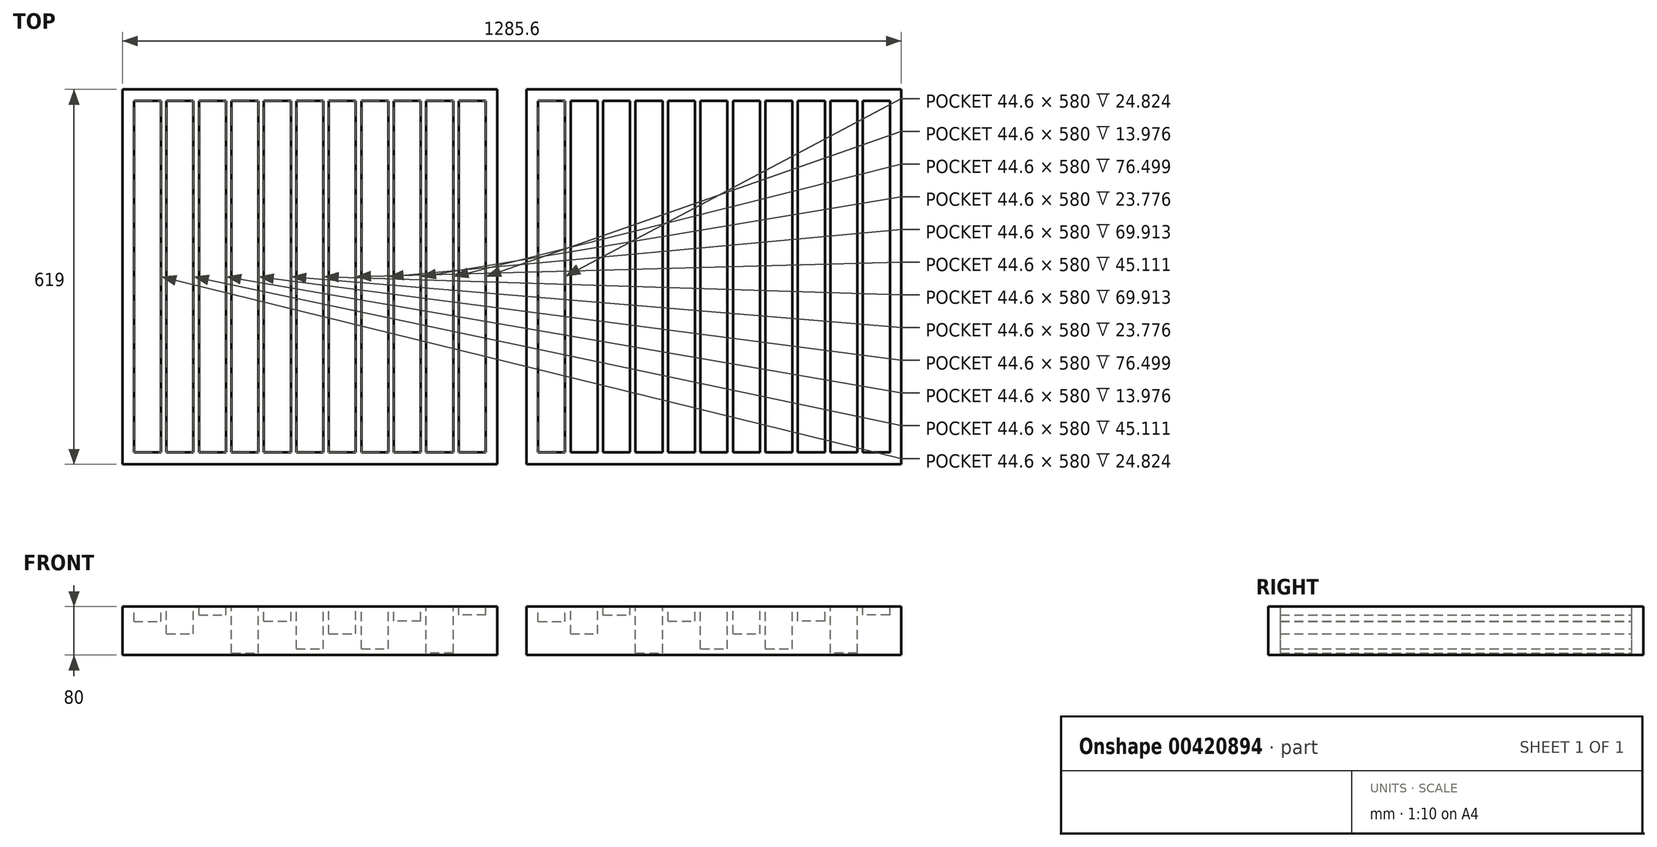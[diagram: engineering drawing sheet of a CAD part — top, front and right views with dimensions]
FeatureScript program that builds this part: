
annotation { "Feature Type Name" : "Feature", "Feature Type Description" : "" }
export const myFeature = defineFeature(function(context is Context, id is Id, definition is map)
    precondition{}
    {
        {
            var Q0;
            Q0=qCreatedBy(makeId("Front.planeOp"),FACE);
            var sketch = newSketch(context, id + "F0", { "sketchPlane" : qUnion([Q0])});
            skLineSegment(sketch, "E0.bottom", {"start": v(0, 0) * mm, "end": v(9, 0) * mm});
            skLineSegment(sketch, "E0.top", {"start": v(0, 80) * mm, "end": v(9, 80) * mm});
            skLineSegment(sketch, "E0.left", {"start": v(0, 0) * mm, "end": v(0, 80) * mm});
            skLineSegment(sketch, "E0.right", {"start": v(9, 0) * mm, "end": v(9, 80) * mm});
            skLineSegment(sketch, "E1.1.0.0", {"start": v(53.6, 80) * mm, "end": v(62.6, 80) * mm});
            skLineSegment(sketch, "E1.1.0.1", {"start": v(62.6, 0) * mm, "end": v(62.6, 80) * mm});
            skLineSegment(sketch, "E1.1.0.2", {"start": v(53.6, 0) * mm, "end": v(62.6, 0) * mm});
            skLineSegment(sketch, "E1.1.0.3", {"start": v(53.6, 0) * mm, "end": v(53.6, 80) * mm});
            skLineSegment(sketch, "E1.2.0.0", {"start": v(107.2, 80) * mm, "end": v(116.2, 80) * mm});
            skLineSegment(sketch, "E1.2.0.1", {"start": v(116.2, 0) * mm, "end": v(116.2, 80) * mm});
            skLineSegment(sketch, "E1.2.0.2", {"start": v(107.2, 0) * mm, "end": v(116.2, 0) * mm});
            skLineSegment(sketch, "E1.2.0.3", {"start": v(107.2, 0) * mm, "end": v(107.2, 80) * mm});
            skLineSegment(sketch, "E1.3.0.0", {"start": v(160.8, 80) * mm, "end": v(169.8, 80) * mm});
            skLineSegment(sketch, "E1.3.0.1", {"start": v(169.8, 0) * mm, "end": v(169.8, 80) * mm});
            skLineSegment(sketch, "E1.3.0.2", {"start": v(160.8, 0) * mm, "end": v(169.8, 0) * mm});
            skLineSegment(sketch, "E1.3.0.3", {"start": v(160.8, 0) * mm, "end": v(160.8, 80) * mm});
            skLineSegment(sketch, "E1.4.0.0", {"start": v(214.4, 80) * mm, "end": v(223.4, 80) * mm});
            skLineSegment(sketch, "E1.4.0.1", {"start": v(223.4, 0) * mm, "end": v(223.4, 80) * mm});
            skLineSegment(sketch, "E1.4.0.2", {"start": v(214.4, 0) * mm, "end": v(223.4, 0) * mm});
            skLineSegment(sketch, "E1.4.0.3", {"start": v(214.4, 0) * mm, "end": v(214.4, 80) * mm});
            skLineSegment(sketch, "E1.5.0.0", {"start": v(268, 80) * mm, "end": v(277, 80) * mm});
            skLineSegment(sketch, "E1.5.0.1", {"start": v(277, 0) * mm, "end": v(277, 80) * mm});
            skLineSegment(sketch, "E1.5.0.2", {"start": v(268, 0) * mm, "end": v(277, 0) * mm});
            skLineSegment(sketch, "E1.5.0.3", {"start": v(268, 0) * mm, "end": v(268, 80) * mm});
            skLineSegment(sketch, "E1.6.0.0", {"start": v(321.6, 80) * mm, "end": v(330.6, 80) * mm});
            skLineSegment(sketch, "E1.6.0.1", {"start": v(330.6, 0) * mm, "end": v(330.6, 80) * mm});
            skLineSegment(sketch, "E1.6.0.2", {"start": v(321.6, 0) * mm, "end": v(330.6, 0) * mm});
            skLineSegment(sketch, "E1.6.0.3", {"start": v(321.6, 0) * mm, "end": v(321.6, 80) * mm});
            skLineSegment(sketch, "E1.7.0.0", {"start": v(375.2, 80) * mm, "end": v(384.2, 80) * mm});
            skLineSegment(sketch, "E1.7.0.1", {"start": v(384.2, 0) * mm, "end": v(384.2, 80) * mm});
            skLineSegment(sketch, "E1.7.0.2", {"start": v(375.2, 0) * mm, "end": v(384.2, 0) * mm});
            skLineSegment(sketch, "E1.7.0.3", {"start": v(375.2, 0) * mm, "end": v(375.2, 80) * mm});
            skLineSegment(sketch, "E1.8.0.0", {"start": v(428.8, 80) * mm, "end": v(437.8, 80) * mm});
            skLineSegment(sketch, "E1.8.0.1", {"start": v(437.8, 0) * mm, "end": v(437.8, 80) * mm});
            skLineSegment(sketch, "E1.8.0.2", {"start": v(428.8, 0) * mm, "end": v(437.8, 0) * mm});
            skLineSegment(sketch, "E1.8.0.3", {"start": v(428.8, 0) * mm, "end": v(428.8, 80) * mm});
            skLineSegment(sketch, "E1.9.0.0", {"start": v(482.4, 80) * mm, "end": v(491.4, 80) * mm});
            skLineSegment(sketch, "E1.9.0.1", {"start": v(491.4, 0) * mm, "end": v(491.4, 80) * mm});
            skLineSegment(sketch, "E1.9.0.2", {"start": v(482.4, 0) * mm, "end": v(491.4, 0) * mm});
            skLineSegment(sketch, "E1.9.0.3", {"start": v(482.4, 0) * mm, "end": v(482.4, 80) * mm});
            skLineSegment(sketch, "E1.10.0.0", {"start": v(536, 80) * mm, "end": v(545, 80) * mm});
            skLineSegment(sketch, "E1.10.0.1", {"start": v(545, 0) * mm, "end": v(545, 80) * mm});
            skLineSegment(sketch, "E1.10.0.2", {"start": v(536, 0) * mm, "end": v(545, 0) * mm});
            skLineSegment(sketch, "E1.10.0.3", {"start": v(536, 0) * mm, "end": v(536, 80) * mm});
            skLineSegment(sketch, "E1.11.0.0", {"start": v(589.6, 80) * mm, "end": v(598.6, 80) * mm});
            skLineSegment(sketch, "E1.11.0.1", {"start": v(598.6, 0) * mm, "end": v(598.6, 80) * mm});
            skLineSegment(sketch, "E1.11.0.2", {"start": v(589.6, 0) * mm, "end": v(598.6, 0) * mm});
            skLineSegment(sketch, "E1.11.0.3", {"start": v(589.6, 0) * mm, "end": v(589.6, 80) * mm});
            skLineSegment(sketch, "E1.direction1", {"start": v(0, 0) * mm, "end": v(53.6, 0) * mm, "construction": true});
            skLineSegment(sketch, "E2", {"start": v(9, 55.18) * mm, "end": v(53.6, 55.18) * mm});
            skLineSegment(sketch, "E3", {"start": v(62.6, 34.89) * mm, "end": v(107.2, 34.89) * mm});
            skLineSegment(sketch, "E4", {"start": v(116.2, 66.02) * mm, "end": v(160.8, 66.02) * mm});
            skLineSegment(sketch, "E5", {"start": v(169.8, 3.5) * mm, "end": v(214.4, 3.5) * mm});
            skLineSegment(sketch, "E6", {"start": v(223.4, 56.22) * mm, "end": v(268, 56.22) * mm});
            skLineSegment(sketch, "E7", {"start": v(589.6, 66.02) * mm, "end": v(545, 66.02) * mm});
            skLineSegment(sketch, "E8", {"start": v(536, 3.5) * mm, "end": v(491.4, 3.5) * mm});
            skPoint(sketch, "E8.startSnap0", {"position": v(192.1, 3.5) * mm});
            skLineSegment(sketch, "E9", {"start": v(482.4, 56.22) * mm, "end": v(437.8, 56.22) * mm});
            skLineSegment(sketch, "E10", {"start": v(330.6, 34.89) * mm, "end": v(375.2, 34.89) * mm});
            skLineSegment(sketch, "E11", {"start": v(277, 10.09) * mm, "end": v(321.6, 10.09) * mm});
            skLineSegment(sketch, "E12", {"start": v(384.2, 10.09) * mm, "end": v(428.8, 10.09) * mm});
            skLineSegment(sketch, "E13", {"start": v(0, 0) * mm, "end": v(598.6, 0) * mm});
            skLineSegment(sketch, "E14", {"start": v(0, 80) * mm, "end": v(598.6, 80) * mm});
            skSolve(sketch);
        }
        {
            var Q0;
            {var subQ3=sQuery(id+"F0.wireOp",EDGE,"E11");Q0=makeQuery(id+"F0.imprint","IMPRINT",FACE,{"disambiguationData":[TD([[makeQuery(id+"F0.imprint","IMPRINT",EDGE,{"derivedFrom":subQ3}),-1.0]])]});}
            var Q1;
            {var subQ6=sQuery(id+"F0.wireOp",EDGE,"E0.left");Q1=makeQuery(id+"F0.imprint","IMPRINT",FACE,{"disambiguationData":[TD([[makeQuery(id+"F0.imprint","IMPRINT",EDGE,{"derivedFrom":subQ6}),-1.0]])]});}
            var Q2;
            {var subQ3=sQuery(id+"F0.wireOp",EDGE,"E2");Q2=makeQuery(id+"F0.imprint","IMPRINT",FACE,{"disambiguationData":[TD([[makeQuery(id+"F0.imprint","IMPRINT",EDGE,{"derivedFrom":subQ3}),-1.0]])]});}
            var Q3;
            {var subQ4=sQuery(id+"F0.wireOp",EDGE,"RwyZLAWs-IkjT-xB0i-7LVW-v5MOJDuku8NZ");var subQ6=sQuery(id+"F0.wireOp",EDGE,"E1.1.0.1");var subQ7=makeQuery(id+"F0.imprint","INTERSECT",VERTEX,{"derivedFrom":[subQ6,subQ4]});Q3=makeQuery(id+"F0.imprint","IMPRINT",FACE,{"disambiguationData":[TD([[makeQuery(id+"F0.imprint","IMPRINT",EDGE,{"disambiguationData":[TD([[subQ7,-1.0]])],"derivedFrom":subQ6}),1.0]])]});}
            var Q4;
            {var subQ3=sQuery(id+"F0.wireOp",EDGE,"E3");Q4=makeQuery(id+"F0.imprint","IMPRINT",FACE,{"disambiguationData":[TD([[makeQuery(id+"F0.imprint","IMPRINT",EDGE,{"derivedFrom":subQ3}),-1.0]])]});}
            var Q5;
            {var subQ4=sQuery(id+"F0.wireOp",EDGE,"RwyZLAWs-IkjT-xB0i-7LVW-v5MOJDuku8NZ");var subQ6=sQuery(id+"F0.wireOp",EDGE,"E1.2.0.1");var subQ9=makeQuery(id+"F0.imprint","INTERSECT",VERTEX,{"derivedFrom":[subQ6,subQ4]});Q5=makeQuery(id+"F0.imprint","IMPRINT",FACE,{"disambiguationData":[TD([[makeQuery(id+"F0.imprint","IMPRINT",EDGE,{"disambiguationData":[TD([[subQ9,-1.0]])],"derivedFrom":subQ6}),1.0]])]});}
            var Q6;
            {var subQ3=sQuery(id+"F0.wireOp",EDGE,"E4");Q6=makeQuery(id+"F0.imprint","IMPRINT",FACE,{"disambiguationData":[TD([[makeQuery(id+"F0.imprint","IMPRINT",EDGE,{"derivedFrom":subQ3}),-1.0]])]});}
            var Q7;
            {var subQ4=sQuery(id+"F0.wireOp",EDGE,"E1.3.0.1");var subQ6=sQuery(id+"F0.wireOp",EDGE,"RwyZLAWs-IkjT-xB0i-7LVW-v5MOJDuku8NZ");var subQ9=makeQuery(id+"F0.imprint","INTERSECT",VERTEX,{"derivedFrom":[subQ4,subQ6]});Q7=makeQuery(id+"F0.imprint","IMPRINT",FACE,{"disambiguationData":[TD([[makeQuery(id+"F0.imprint","IMPRINT",EDGE,{"disambiguationData":[TD([[subQ9,-1.0]])],"derivedFrom":subQ4}),1.0]])]});}
            var Q8;
            {var subQ3=sQuery(id+"F0.wireOp",EDGE,"E5");Q8=makeQuery(id+"F0.imprint","IMPRINT",FACE,{"disambiguationData":[TD([[makeQuery(id+"F0.imprint","IMPRINT",EDGE,{"derivedFrom":subQ3}),-1.0]])]});}
            var Q9;
            {var subQ4=sQuery(id+"F0.wireOp",EDGE,"RwyZLAWs-IkjT-xB0i-7LVW-v5MOJDuku8NZ");var subQ6=sQuery(id+"F0.wireOp",EDGE,"E1.4.0.1");var subQ9=makeQuery(id+"F0.imprint","INTERSECT",VERTEX,{"derivedFrom":[subQ6,subQ4]});Q9=makeQuery(id+"F0.imprint","IMPRINT",FACE,{"disambiguationData":[TD([[makeQuery(id+"F0.imprint","IMPRINT",EDGE,{"disambiguationData":[TD([[subQ9,-1.0]])],"derivedFrom":subQ6}),1.0]])]});}
            var Q10;
            {var subQ3=sQuery(id+"F0.wireOp",EDGE,"E6");Q10=makeQuery(id+"F0.imprint","IMPRINT",FACE,{"disambiguationData":[TD([[makeQuery(id+"F0.imprint","IMPRINT",EDGE,{"derivedFrom":subQ3}),-1.0]])]});}
            var Q11;
            {var subQ4=sQuery(id+"F0.wireOp",EDGE,"RwyZLAWs-IkjT-xB0i-7LVW-v5MOJDuku8NZ");var subQ6=sQuery(id+"F0.wireOp",EDGE,"E1.5.0.1");var subQ9=makeQuery(id+"F0.imprint","INTERSECT",VERTEX,{"derivedFrom":[subQ6,subQ4]});Q11=makeQuery(id+"F0.imprint","IMPRINT",FACE,{"disambiguationData":[TD([[makeQuery(id+"F0.imprint","IMPRINT",EDGE,{"disambiguationData":[TD([[subQ9,-1.0]])],"derivedFrom":subQ6}),1.0]])]});}
            var Q12;
            {var subQ4=sQuery(id+"F0.wireOp",EDGE,"RwyZLAWs-IkjT-xB0i-7LVW-v5MOJDuku8NZ");var subQ5=sQuery(id+"F0.wireOp",EDGE,"E1.6.0.1");var subQ6=makeQuery(id+"F0.imprint","INTERSECT",VERTEX,{"derivedFrom":[subQ5,subQ4]});Q12=makeQuery(id+"F0.imprint","IMPRINT",FACE,{"disambiguationData":[TD([[makeQuery(id+"F0.imprint","IMPRINT",EDGE,{"disambiguationData":[TD([[subQ6,-1.0]])],"derivedFrom":subQ5}),1.0]])]});}
            var Q13;
            {var subQ3=sQuery(id+"F0.wireOp",EDGE,"E10");Q13=makeQuery(id+"F0.imprint","IMPRINT",FACE,{"disambiguationData":[TD([[makeQuery(id+"F0.imprint","IMPRINT",EDGE,{"derivedFrom":subQ3}),-1.0]])]});}
            var Q14;
            {var subQ4=sQuery(id+"F0.wireOp",EDGE,"RwyZLAWs-IkjT-xB0i-7LVW-v5MOJDuku8NZ");var subQ6=sQuery(id+"F0.wireOp",EDGE,"E1.7.0.1");var subQ9=makeQuery(id+"F0.imprint","INTERSECT",VERTEX,{"derivedFrom":[subQ6,subQ4]});Q14=makeQuery(id+"F0.imprint","IMPRINT",FACE,{"disambiguationData":[TD([[makeQuery(id+"F0.imprint","IMPRINT",EDGE,{"disambiguationData":[TD([[subQ9,-1.0]])],"derivedFrom":subQ6}),1.0]])]});}
            var Q15;
            {var subQ4=sQuery(id+"F0.wireOp",EDGE,"RwyZLAWs-IkjT-xB0i-7LVW-v5MOJDuku8NZ");var subQ6=sQuery(id+"F0.wireOp",EDGE,"E1.8.0.1");var subQ9=makeQuery(id+"F0.imprint","INTERSECT",VERTEX,{"derivedFrom":[subQ6,subQ4]});Q15=makeQuery(id+"F0.imprint","IMPRINT",FACE,{"disambiguationData":[TD([[makeQuery(id+"F0.imprint","IMPRINT",EDGE,{"disambiguationData":[TD([[subQ9,-1.0]])],"derivedFrom":subQ6}),1.0]])]});}
            var Q16;
            {var subQ3=sQuery(id+"F0.wireOp",EDGE,"E9");Q16=makeQuery(id+"F0.imprint","IMPRINT",FACE,{"disambiguationData":[TD([[makeQuery(id+"F0.imprint","IMPRINT",EDGE,{"derivedFrom":subQ3}),1.0]])]});}
            var Q17;
            {var subQ4=sQuery(id+"F0.wireOp",EDGE,"RwyZLAWs-IkjT-xB0i-7LVW-v5MOJDuku8NZ");var subQ6=sQuery(id+"F0.wireOp",EDGE,"E1.9.0.1");var subQ9=makeQuery(id+"F0.imprint","INTERSECT",VERTEX,{"derivedFrom":[subQ6,subQ4]});Q17=makeQuery(id+"F0.imprint","IMPRINT",FACE,{"disambiguationData":[TD([[makeQuery(id+"F0.imprint","IMPRINT",EDGE,{"disambiguationData":[TD([[subQ9,-1.0]])],"derivedFrom":subQ6}),1.0]])]});}
            var Q18;
            {var subQ3=sQuery(id+"F0.wireOp",EDGE,"E8");Q18=makeQuery(id+"F0.imprint","IMPRINT",FACE,{"disambiguationData":[TD([[makeQuery(id+"F0.imprint","IMPRINT",EDGE,{"derivedFrom":subQ3}),1.0]])]});}
            var Q19;
            {var subQ4=sQuery(id+"F0.wireOp",EDGE,"RwyZLAWs-IkjT-xB0i-7LVW-v5MOJDuku8NZ");var subQ6=sQuery(id+"F0.wireOp",EDGE,"E1.10.0.1");var subQ9=makeQuery(id+"F0.imprint","INTERSECT",VERTEX,{"derivedFrom":[subQ6,subQ4]});Q19=makeQuery(id+"F0.imprint","IMPRINT",FACE,{"disambiguationData":[TD([[makeQuery(id+"F0.imprint","IMPRINT",EDGE,{"disambiguationData":[TD([[subQ9,-1.0]])],"derivedFrom":subQ6}),1.0]])]});}
            var Q20;
            {var subQ3=sQuery(id+"F0.wireOp",EDGE,"E7");Q20=makeQuery(id+"F0.imprint","IMPRINT",FACE,{"disambiguationData":[TD([[makeQuery(id+"F0.imprint","IMPRINT",EDGE,{"derivedFrom":subQ3}),1.0]])]});}
            var Q21;
            {var subQ4=sQuery(id+"F0.wireOp",EDGE,"RwyZLAWs-IkjT-xB0i-7LVW-v5MOJDuku8NZ");var subQ6=sQuery(id+"F0.wireOp",EDGE,"E1.11.0.1");var subQ9=makeQuery(id+"F0.imprint","INTERSECT",VERTEX,{"derivedFrom":[subQ6,subQ4]});Q21=makeQuery(id+"F0.imprint","IMPRINT",FACE,{"disambiguationData":[TD([[makeQuery(id+"F0.imprint","IMPRINT",EDGE,{"disambiguationData":[TD([[subQ9,-1.0]])],"derivedFrom":subQ6}),1.0]])]});}
            var Q22;
            {var subQ3=sQuery(id+"F0.wireOp",EDGE,"QDkUnuJY-H8uB-LQRV-5p4X-Az3B3ou244IQ");Q22=makeQuery(id+"F0.imprint","IMPRINT",FACE,{"disambiguationData":[TD([[makeQuery(id+"F0.imprint","IMPRINT",EDGE,{"derivedFrom":subQ3}),1.0]])]});}
            var Q23;
            {var subQ4=sQuery(id+"F0.wireOp",EDGE,"c455265c-4ce7-41d5-8e05-9c11a3bf2246.3.11.0");var subQ6=sQuery(id+"F0.wireOp",EDGE,"RwyZLAWs-IkjT-xB0i-7LVW-v5MOJDuku8NZ");var subQ9=makeQuery(id+"F0.imprint","INTERSECT",VERTEX,{"derivedFrom":[subQ4,subQ6]});Q23=makeQuery(id+"F0.imprint","IMPRINT",FACE,{"disambiguationData":[TD([[makeQuery(id+"F0.imprint","IMPRINT",EDGE,{"disambiguationData":[TD([[subQ9,-1.0]])],"derivedFrom":subQ4}),1.0]])]});}
            var Q24;
            {var subQ3=sQuery(id+"F0.wireOp",EDGE,"WxUK2kOJ-jrxP-pgZT-nzD5-Vg9UTsvjE4ji");Q24=makeQuery(id+"F0.imprint","IMPRINT",FACE,{"disambiguationData":[TD([[makeQuery(id+"F0.imprint","IMPRINT",EDGE,{"derivedFrom":subQ3}),-1.0]])]});}
            var Q25;
            {var subQ1=sQuery(id+"F0.wireOp",EDGE,"6b18c773-8643-46cd-9ae8-48085646cfae.3.12.0");Q25=makeQuery(id+"F0.imprint","IMPRINT",FACE,{"disambiguationData":[TD([[makeQuery(id+"F0.imprint","IMPRINT",EDGE,{"derivedFrom":subQ1}),1.0]])]});}
            var Q26;
            {var subQ3=sQuery(id+"F0.wireOp",EDGE,"E12");Q26=makeQuery(id+"F0.imprint","IMPRINT",FACE,{"disambiguationData":[TD([[makeQuery(id+"F0.imprint","IMPRINT",EDGE,{"derivedFrom":subQ3}),-1.0]])]});}
            extrude(context, id + "F1", {"entities" : qUnion([Q0, Q1, Q2, Q3, Q4, Q5, Q6, Q7, Q8, Q9, Q10, Q11, Q12, Q13, Q14, Q15, Q16, Q17, Q18, Q19, Q20, Q21, Q22, Q23, Q24, Q25, Q26]), "depth" : 580 * mm});
        }
        {
            var Q0;
            Q0 = qSketchRegion(id + "F0", true);
            extrude(context, id + "F2", {"entities" : qUnion([Q0]), "operationType" : NewBodyOperationType.ADD, "oppositeDirection" : true, "depth" : 9 * mm});
        }
        {
            var Q0;
            Q0 = qSketchRegion(id + "F0", true);
            var Q1;
            Q1=makeQuery(id+"F1.opExtrude","CAP_VERTEX",VERTEX,{"disambiguationData":[OSD([sQuery(id+"F0.wireOp",EDGE,"E0.left"),sQuery(id+"F0.wireOp",EDGE,"bcZIO9kF-9Tbn-Df1j-lN5f-S5Wp7413Y2EX")])],"isStart":false});
            extrude(context, id + "F3", {"entities" : qUnion([Q0]), "operationType" : NewBodyOperationType.ADD, "endBoundEntityVertex" : qUnion([Q1]), "depth" : 590 * mm, "hasSecondDirection" : true, "secondDirectionOppositeDirection" : false, "secondDirectionDepth" : 580 * mm});
        }
        {
            var Q0;
            {var subQ0=sQuery(id+"F0.wireOp",EDGE,"E14");Q0=makeQuery(id+"F3.boolean.opBoolean","MERGE",FACE,{"derivedFrom":[makeQuery(id+"F2.boolean.opBoolean","MERGE",FACE,{"derivedFrom":[makeQuery(id+"F1.opExtrude","SWEPT_FACE",FACE,{"disambiguationData":[OSD([subQ0]),TDD([makeQuery(id+"F0.imprint","IMPRINT",EDGE,{"disambiguationData":[TD([[makeQuery(id+"F0.imprint","INTERSECT",VERTEX,{"derivedFrom":[sQuery(id+"F0.wireOp",EDGE,"E0.left"),subQ0]}),-1.0]])],"derivedFrom":subQ0})])]}),makeQuery(id+"F1.opExtrude","SWEPT_FACE",FACE,{"disambiguationData":[OSD([subQ0]),TDD([makeQuery(id+"F0.imprint","IMPRINT",EDGE,{"disambiguationData":[TD([[makeQuery(id+"F0.imprint","INTERSECT",VERTEX,{"derivedFrom":[sQuery(id+"F0.wireOp",EDGE,"E1.1.0.1"),subQ0]}),1.0]])],"derivedFrom":subQ0})])]}),makeQuery(id+"F1.opExtrude","SWEPT_FACE",FACE,{"disambiguationData":[OSD([subQ0]),TDD([makeQuery(id+"F0.imprint","IMPRINT",EDGE,{"disambiguationData":[TD([[makeQuery(id+"F0.imprint","INTERSECT",VERTEX,{"derivedFrom":[sQuery(id+"F0.wireOp",EDGE,"E1.2.0.1"),subQ0]}),1.0]])],"derivedFrom":subQ0})])]}),makeQuery(id+"F1.opExtrude","SWEPT_FACE",FACE,{"disambiguationData":[OSD([subQ0]),TDD([makeQuery(id+"F0.imprint","IMPRINT",EDGE,{"disambiguationData":[TD([[makeQuery(id+"F0.imprint","INTERSECT",VERTEX,{"derivedFrom":[sQuery(id+"F0.wireOp",EDGE,"E1.3.0.1"),subQ0]}),1.0]])],"derivedFrom":subQ0})])]}),makeQuery(id+"F1.opExtrude","SWEPT_FACE",FACE,{"disambiguationData":[OSD([subQ0]),TDD([makeQuery(id+"F0.imprint","IMPRINT",EDGE,{"disambiguationData":[TD([[makeQuery(id+"F0.imprint","INTERSECT",VERTEX,{"derivedFrom":[sQuery(id+"F0.wireOp",EDGE,"E1.4.0.1"),subQ0]}),1.0]])],"derivedFrom":subQ0})])]}),makeQuery(id+"F1.opExtrude","SWEPT_FACE",FACE,{"disambiguationData":[OSD([subQ0]),TDD([makeQuery(id+"F0.imprint","IMPRINT",EDGE,{"disambiguationData":[TD([[makeQuery(id+"F0.imprint","INTERSECT",VERTEX,{"derivedFrom":[sQuery(id+"F0.wireOp",EDGE,"E1.5.0.1"),subQ0]}),1.0]])],"derivedFrom":subQ0})])]}),makeQuery(id+"F1.opExtrude","SWEPT_FACE",FACE,{"disambiguationData":[OSD([subQ0]),TDD([makeQuery(id+"F0.imprint","IMPRINT",EDGE,{"disambiguationData":[TD([[makeQuery(id+"F0.imprint","INTERSECT",VERTEX,{"derivedFrom":[sQuery(id+"F0.wireOp",EDGE,"E1.6.0.1"),subQ0]}),1.0]])],"derivedFrom":subQ0})])]}),makeQuery(id+"F1.opExtrude","SWEPT_FACE",FACE,{"disambiguationData":[OSD([subQ0]),TDD([makeQuery(id+"F0.imprint","IMPRINT",EDGE,{"disambiguationData":[TD([[makeQuery(id+"F0.imprint","INTERSECT",VERTEX,{"derivedFrom":[sQuery(id+"F0.wireOp",EDGE,"E1.7.0.1"),subQ0]}),1.0]])],"derivedFrom":subQ0})])]}),makeQuery(id+"F1.opExtrude","SWEPT_FACE",FACE,{"disambiguationData":[OSD([subQ0]),TDD([makeQuery(id+"F0.imprint","IMPRINT",EDGE,{"disambiguationData":[TD([[makeQuery(id+"F0.imprint","INTERSECT",VERTEX,{"derivedFrom":[sQuery(id+"F0.wireOp",EDGE,"E1.8.0.1"),subQ0]}),1.0]])],"derivedFrom":subQ0})])]}),makeQuery(id+"F1.opExtrude","SWEPT_FACE",FACE,{"disambiguationData":[OSD([subQ0]),TDD([makeQuery(id+"F0.imprint","IMPRINT",EDGE,{"disambiguationData":[TD([[makeQuery(id+"F0.imprint","INTERSECT",VERTEX,{"derivedFrom":[sQuery(id+"F0.wireOp",EDGE,"E1.9.0.1"),subQ0]}),1.0]])],"derivedFrom":subQ0})])]}),makeQuery(id+"F1.opExtrude","SWEPT_FACE",FACE,{"disambiguationData":[OSD([subQ0]),TDD([makeQuery(id+"F0.imprint","IMPRINT",EDGE,{"disambiguationData":[TD([[makeQuery(id+"F0.imprint","INTERSECT",VERTEX,{"derivedFrom":[sQuery(id+"F0.wireOp",EDGE,"E1.10.0.1"),subQ0]}),1.0]])],"derivedFrom":subQ0})])]}),makeQuery(id+"F1.opExtrude","SWEPT_FACE",FACE,{"disambiguationData":[OSD([subQ0]),TDD([makeQuery(id+"F0.imprint","IMPRINT",EDGE,{"disambiguationData":[TD([[makeQuery(id+"F0.imprint","INTERSECT",VERTEX,{"derivedFrom":[sQuery(id+"F0.wireOp",EDGE,"E1.11.0.1"),subQ0]}),1.0]])],"derivedFrom":subQ0})])]}),makeQuery(id+"F2.opExtrude","SWEPT_FACE",FACE,{"disambiguationData":[OSD([subQ0])]})]}),makeQuery(id+"F3.opExtrude","SWEPT_FACE",FACE,{"disambiguationData":[OSD([subQ0])]})]});}
            var sketch = newSketch(context, id + "F4", { "sketchPlane" : qUnion([Q0])});
            skLineSegment(sketch, "E15.0", {"start": v(598.6, -590) * mm, "end": v(598.6, 9) * mm});
            skLineSegment(sketch, "E16.0", {"start": v(0, -590) * mm, "end": v(598.6, -590) * mm});
            skLineSegment(sketch, "E17.0", {"start": v(0, -590) * mm, "end": v(0, 9) * mm});
            skLineSegment(sketch, "E18.0", {"start": v(0, 9) * mm, "end": v(598.6, 9) * mm});
            skLineSegment(sketch, "E19.0", {"start": v(608.6, -600) * mm, "end": v(608.6, 19) * mm});
            skLineSegment(sketch, "E19.1", {"start": v(-10, -600) * mm, "end": v(608.6, -600) * mm});
            skLineSegment(sketch, "E19.2", {"start": v(-10, -600) * mm, "end": v(-10, 19) * mm});
            skLineSegment(sketch, "E19.3", {"start": v(-10, 19) * mm, "end": v(608.6, 19) * mm});
            skSolve(sketch);
        }
        {
            var Q0;
            Q0 = qSketchRegion(id + "F4", true);
            var Q1;
            Q1=makeQuery(id+"F3.opExtrude","CAP_VERTEX",VERTEX,{"disambiguationData":[OSD([sQuery(id+"F0.wireOp",EDGE,"E0.left"),sQuery(id+"F0.wireOp",EDGE,"E13")])],"isStart":false});
            extrude(context, id + "F5", {"entities" : qUnion([Q0]), "operationType" : NewBodyOperationType.ADD, "endBound" : BoundingType.UP_TO_VERTEX, "oppositeDirection" : true, "endBoundEntityVertex" : qUnion([Q1]), "depth" : 25 * mm});
        }
        {
            var Q0;
            Q0=makeQuery(id+"F1.opExtrude","SWEPT_BODY",BODY,{"disambiguationData":[OSD([sQuery(id+"F0.wireOp",EDGE,"E0.left"),sQuery(id+"F0.wireOp",EDGE,"E0.right"),sQuery(id+"F0.wireOp",EDGE,"E1.1.0.1"),sQuery(id+"F0.wireOp",EDGE,"E1.1.0.3"),sQuery(id+"F0.wireOp",EDGE,"E1.2.0.1"),sQuery(id+"F0.wireOp",EDGE,"E1.2.0.3"),sQuery(id+"F0.wireOp",EDGE,"E1.3.0.1"),sQuery(id+"F0.wireOp",EDGE,"E1.3.0.3"),sQuery(id+"F0.wireOp",EDGE,"E1.4.0.1"),sQuery(id+"F0.wireOp",EDGE,"E1.4.0.3"),sQuery(id+"F0.wireOp",EDGE,"E1.5.0.1"),sQuery(id+"F0.wireOp",EDGE,"E1.5.0.3"),sQuery(id+"F0.wireOp",EDGE,"E1.6.0.1"),sQuery(id+"F0.wireOp",EDGE,"E1.6.0.3"),sQuery(id+"F0.wireOp",EDGE,"E1.7.0.1"),sQuery(id+"F0.wireOp",EDGE,"E1.7.0.3"),sQuery(id+"F0.wireOp",EDGE,"E1.8.0.1"),sQuery(id+"F0.wireOp",EDGE,"E1.8.0.3"),sQuery(id+"F0.wireOp",EDGE,"E1.9.0.1"),sQuery(id+"F0.wireOp",EDGE,"E1.9.0.3"),sQuery(id+"F0.wireOp",EDGE,"E1.10.0.1"),sQuery(id+"F0.wireOp",EDGE,"E1.10.0.3"),sQuery(id+"F0.wireOp",EDGE,"E1.11.0.1"),sQuery(id+"F0.wireOp",EDGE,"E1.11.0.3"),sQuery(id+"F0.wireOp",EDGE,"E2"),sQuery(id+"F0.wireOp",EDGE,"E3"),sQuery(id+"F0.wireOp",EDGE,"E4"),sQuery(id+"F0.wireOp",EDGE,"E5"),sQuery(id+"F0.wireOp",EDGE,"E6"),sQuery(id+"F0.wireOp",EDGE,"E7"),sQuery(id+"F0.wireOp",EDGE,"E8"),sQuery(id+"F0.wireOp",EDGE,"E9"),sQuery(id+"F0.wireOp",EDGE,"E10"),sQuery(id+"F0.wireOp",EDGE,"E11"),sQuery(id+"F0.wireOp",EDGE,"E12"),sQuery(id+"F0.wireOp",EDGE,"E13"),sQuery(id+"F0.wireOp",EDGE,"E14")])]});
            transform(context, id + "F6", {"entities" : qUnion([Q0]), "transformType" : TransformType.TRANSLATION_3D, "dx" : 667 * mm, "dy" : 0 * mm, "dz" : 0 * mm, "makeCopy" : true});
        }
    });
